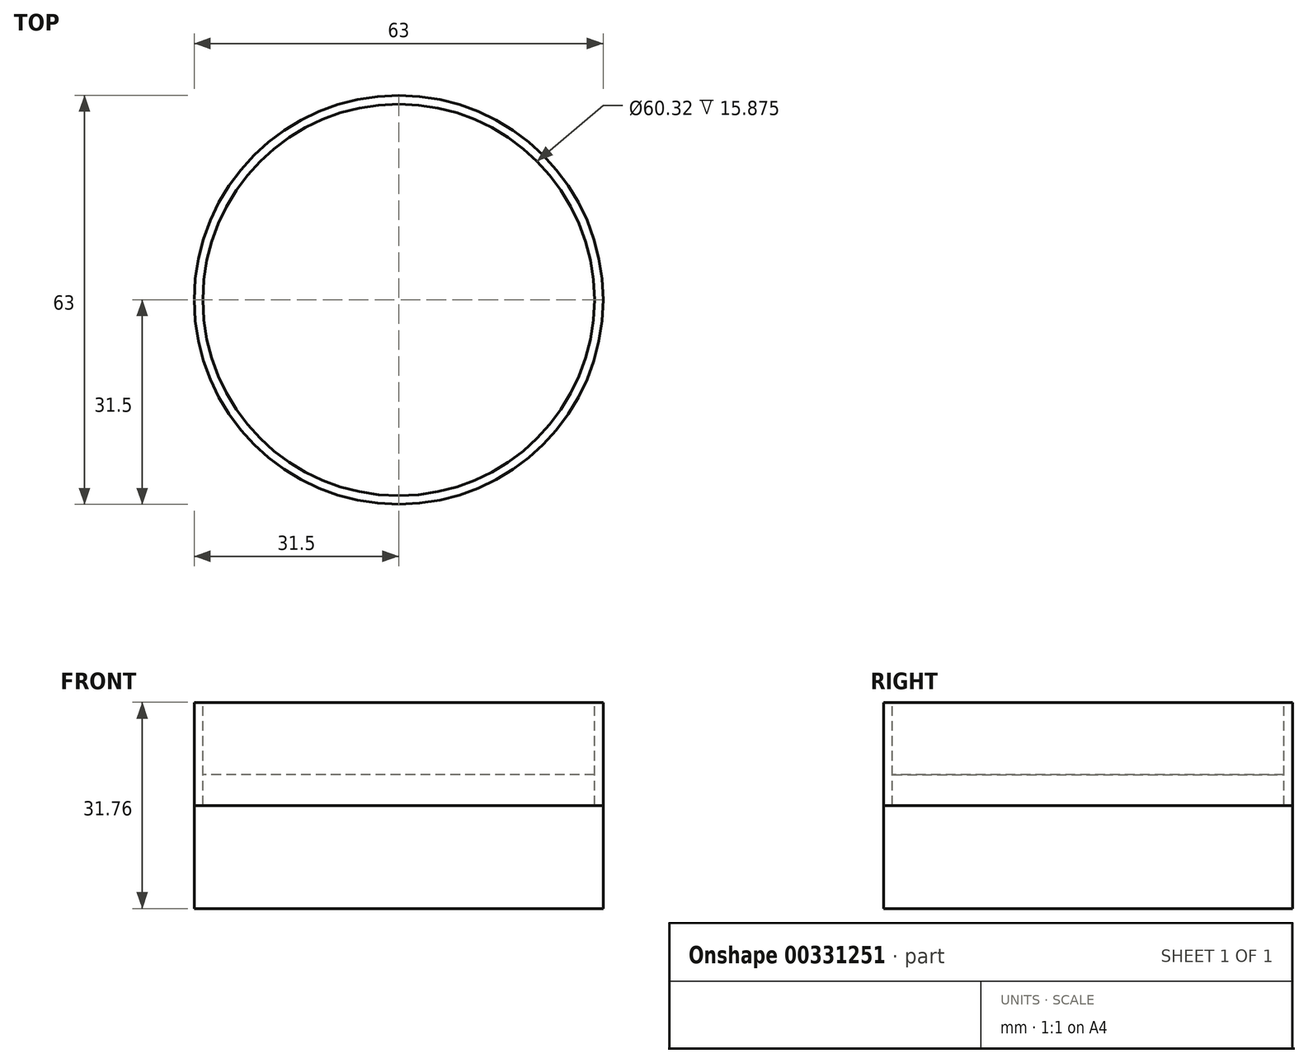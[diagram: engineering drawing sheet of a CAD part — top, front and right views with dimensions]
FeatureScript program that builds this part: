
annotation { "Feature Type Name" : "Feature", "Feature Type Description" : "" }
export const myFeature = defineFeature(function(context is Context, id is Id, definition is map)
    precondition{}
    {
        {
            var Q0;
            Q0=qCreatedBy(makeId("Front.planeOp"),FACE);
            var sketch = newSketch(context, id + "F0", { "sketchPlane" : qUnion([Q0])});
            skLineSegment(sketch, "E0.bottom", {"start": v(-31.75, 15.88) * mm, "end": v(31.75, 15.88) * mm});
            skLineSegment(sketch, "E0.top", {"start": v(-31.75, -15.88) * mm, "end": v(31.75, -15.88) * mm});
            skLineSegment(sketch, "E0.left", {"start": v(-31.75, 15.88) * mm, "end": v(-31.75, -15.88) * mm});
            skLineSegment(sketch, "E0.right", {"start": v(31.75, 15.88) * mm, "end": v(31.75, -15.88) * mm});
            skPoint(sketch, "E0.middle", {"position": v(0, 0) * mm});
            skLineSegment(sketch, "E1", {"start": v(-31.75, 0) * mm, "end": v(31.75, 0) * mm});
            skLineSegment(sketch, "E2", {"start": v(-30.16, 15.87) * mm, "end": v(-30.16, 0) * mm});
            skLineSegment(sketch, "E3", {"start": v(-30.16, 4.76) * mm, "end": v(0, 4.76) * mm});
            skLineSegment(sketch, "E4", {"start": v(0, 0) * mm, "end": v(0, -14.84) * mm, "construction": true});
            skLineSegment(sketch, "E5.MirrorCS", {"start": v(30.16, 15.88) * mm, "end": v(30.16, 0) * mm});
            skLineSegment(sketch, "E6.MirrorCS", {"start": v(30.16, 4.76) * mm, "end": v(0, 4.76) * mm});
            skSolve(sketch);
        }
        {
            var Q0;
            Q0=qCreatedBy(makeId("Front.planeOp"),FACE);
            var sketch = newSketch(context, id + "F1", { "sketchPlane" : qUnion([Q0])});
            skLineSegment(sketch, "E7", {"start": v(0, 0) * mm, "end": v(0, -32.02) * mm, "construction": true});
            skLineSegment(sketch, "E8.0", {"start": v(30.16, 4.76) * mm, "end": v(0, 4.76) * mm});
            skLineSegment(sketch, "E9.0", {"start": v(0, -15.88) * mm, "end": v(31.75, -15.88) * mm});
            skPoint(sketch, "E10.orphan", {"position": v(-31.75, -15.88) * mm});
            skLineSegment(sketch, "E11", {"start": v(30.16, 4.76) * mm, "end": v(30.16, 0) * mm});
            skLineSegment(sketch, "E12", {"start": v(30.16, 0) * mm, "end": v(31.75, 0) * mm});
            skLineSegment(sketch, "E13", {"start": v(31.75, 0) * mm, "end": v(31.75, -15.88) * mm});
            skLineSegment(sketch, "E14", {"start": v(0, 4.76) * mm, "end": v(0, -15.88) * mm});
            skSolve(sketch);
        }
        {
            var Q0;
            Q0 = qSketchRegion(id + "F1", true);
            var Q1;
            Q1=sQuery(id+"F1.wireOp",EDGE,"E7");
            revolve(context, id + "F2", {"entities" : qUnion([Q0]), "axis" : qUnion([Q1]), "revolveType" : RevolveType.FULL});
        }
        {
            var Q0;
            Q0=qCreatedBy(makeId("Front.planeOp"),FACE);
            var sketch = newSketch(context, id + "F3", { "sketchPlane" : qUnion([Q0])});
            skLineSegment(sketch, "E15.0", {"start": v(30.16, 15.88) * mm, "end": v(30.16, 0) * mm});
            skLineSegment(sketch, "E15.1", {"start": v(31.75, 15.88) * mm, "end": v(31.75, 0) * mm});
            skLineSegment(sketch, "E16", {"start": v(30.16, 0) * mm, "end": v(31.75, 0) * mm});
            skPoint(sketch, "E17.orphan", {"position": v(31.75, -15.88) * mm});
            skLineSegment(sketch, "E18", {"start": v(30.16, 15.88) * mm, "end": v(31.75, 15.88) * mm});
            skLineSegment(sketch, "E19", {"start": v(0, 0) * mm, "end": v(0, -26.7) * mm, "construction": true});
            skSolve(sketch);
        }
        {
            var Q0;
            Q0 = qSketchRegion(id + "F3", true);
            var Q1;
            Q1=sQuery(id+"F3.wireOp",EDGE,"E19");
            revolve(context, id + "F4", {"entities" : qUnion([Q0]), "axis" : qUnion([Q1]), "revolveType" : RevolveType.FULL});
        }
        {
            var Q0;
            Q0=makeQuery(id+"F4.opRevolve","SWEPT_FACE",FACE,{"disambiguationData":[OSD([sQuery(id+"F3.wireOp",EDGE,"E18")])]});
            var sketch = newSketch(context, id + "F5", { "sketchPlane" : qUnion([Q0])});
            skCircle(sketch, "E20.0", {"center": v(0, 0) * mm, "radius": 31.75 * mm});
            skCircle(sketch, "E21.0", {"center": v(0, 0) * mm, "radius": 31.5 * mm});
            skSolve(sketch);
        }
        {
            var Q0;
            Q0 = qSketchRegion(id + "F5", true);
            extrude(context, id + "F6", {"entities" : qUnion([Q0]), "operationType" : NewBodyOperationType.REMOVE, "endBound" : BoundingType.THROUGH_ALL, "oppositeDirection" : true, "depth" : 25.4 * mm});
        }
    });
